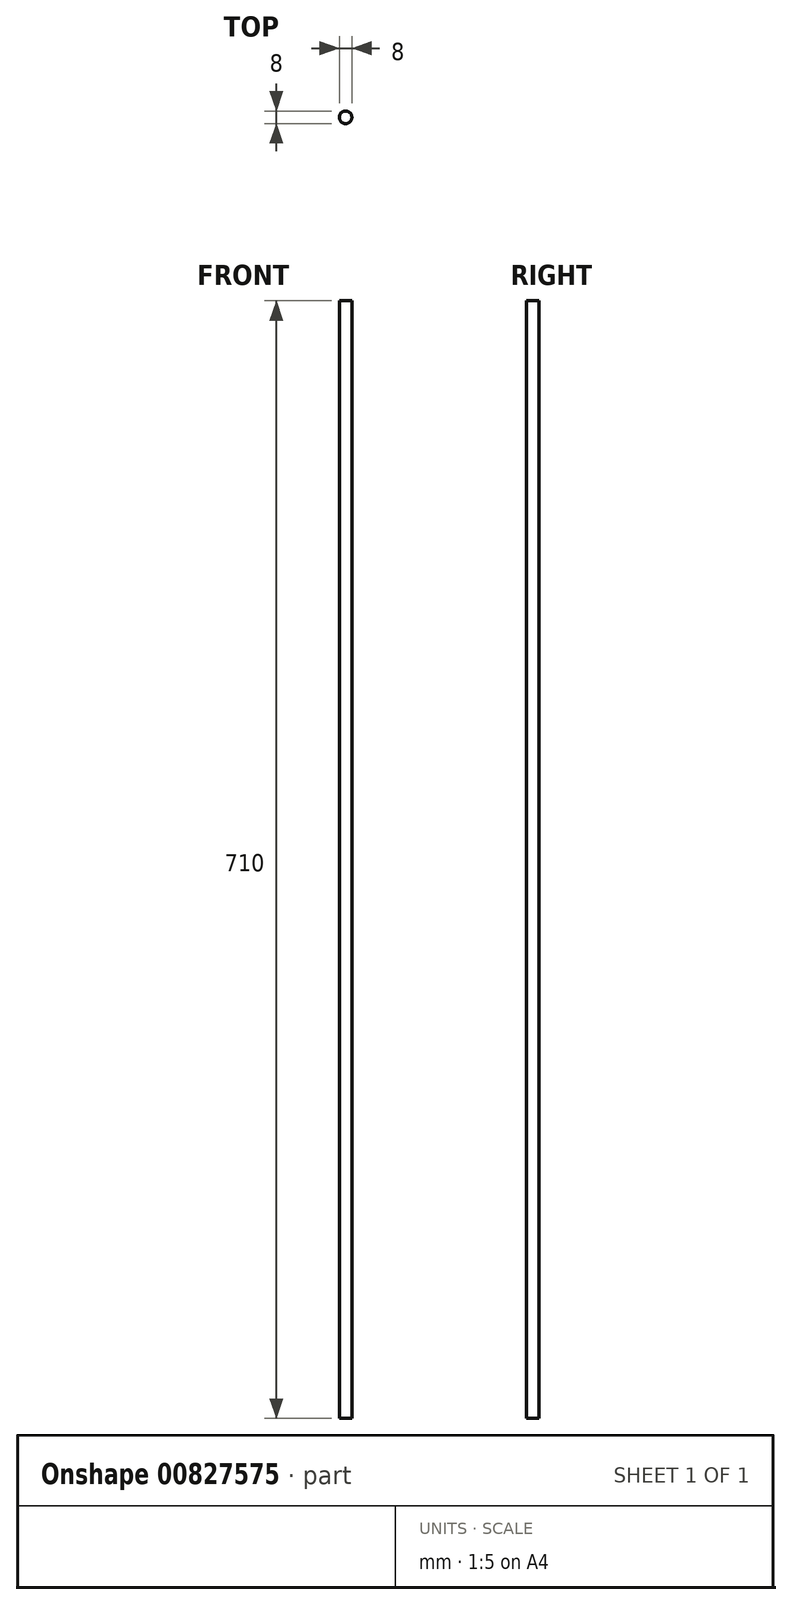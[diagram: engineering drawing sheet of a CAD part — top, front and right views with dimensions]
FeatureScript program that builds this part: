
annotation { "Feature Type Name" : "Feature", "Feature Type Description" : "" }
export const myFeature = defineFeature(function(context is Context, id is Id, definition is map)
    precondition{}
    {
        {
            var Q0;
            Q0=qCreatedBy(makeId("Top.planeOp"),FACE);
            var sketch = newSketch(context, id + "F0", { "sketchPlane" : qUnion([Q0])});
            skCircle(sketch, "E0", {"center": v(0, 0) * mm, "radius": 4 * mm});
            skSolve(sketch);
        }
        {
            var Q0;
            Q0=makeQuery(id+"F0.imprint","IMPRINT",FACE,{"disambiguationData":[TD([[makeQuery(id+"F0.imprint","IMPRINT",EDGE,{"derivedFrom":sQuery(id+"F0.wireOp",EDGE,"E0")}),1.0]])]});
            extrude(context, id + "F1", {"entities" : qUnion([Q0]), "depth" : 710 * mm, "offsetDistance" : 25 * mm});
        }
    });
